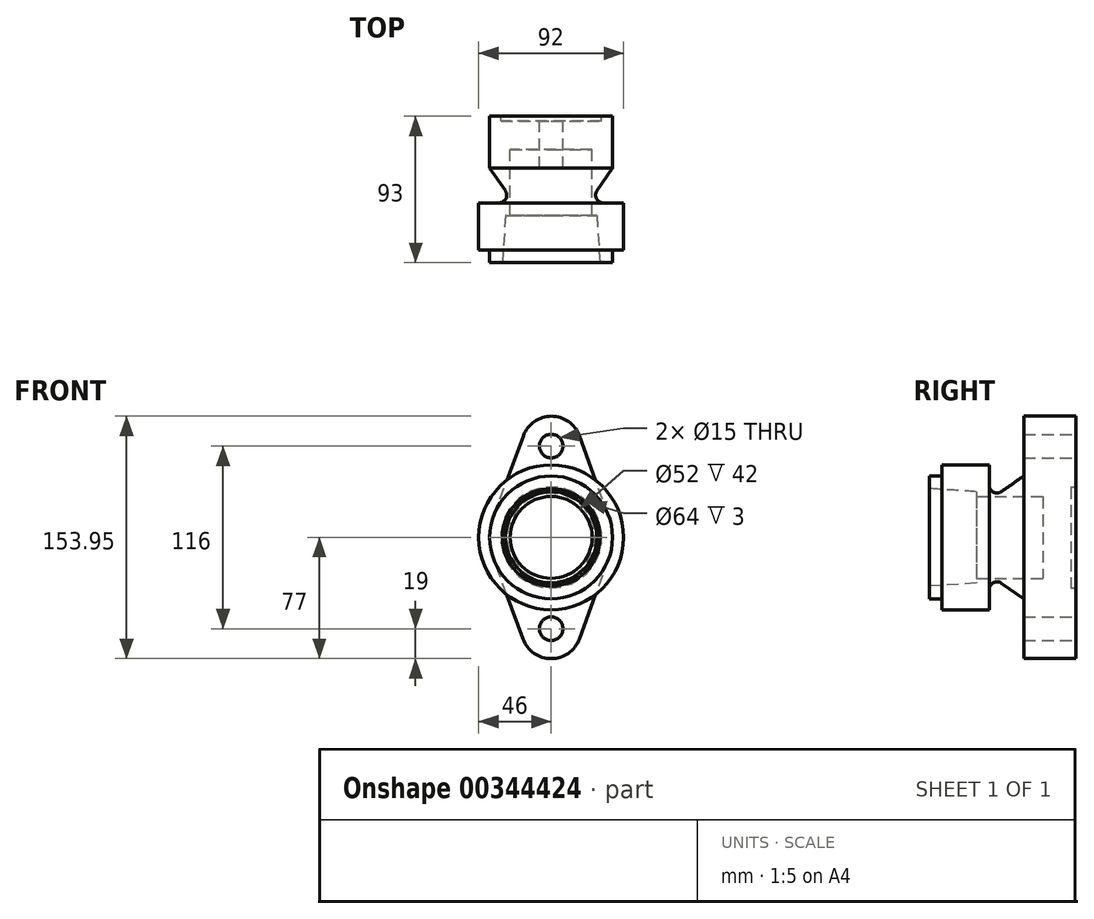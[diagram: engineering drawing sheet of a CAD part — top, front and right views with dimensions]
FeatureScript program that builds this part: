
annotation { "Feature Type Name" : "Feature", "Feature Type Description" : "" }
export const myFeature = defineFeature(function(context is Context, id is Id, definition is map)
    precondition{}
    {
        {
            var Q0;
            Q0=qCreatedBy(makeId("Right.planeOp"),FACE);
            var sketch = newSketch(context, id + "F0", { "sketchPlane" : qUnion([Q0])});
            skLineSegment(sketch, "E0", {"start": v(0, 0) * mm, "end": v(18, 0) * mm});
            skLineSegment(sketch, "E1", {"start": v(18, 0) * mm, "end": v(18, 32) * mm});
            skLineSegment(sketch, "E2", {"start": v(18, 32) * mm, "end": v(21, 32) * mm});
            skLineSegment(sketch, "E3", {"start": v(21, 32) * mm, "end": v(21, 39) * mm});
            skLineSegment(sketch, "E4", {"start": v(-64, 46) * mm, "end": v(-64, 39) * mm});
            skLineSegment(sketch, "E5", {"start": v(-64, 39) * mm, "end": v(-72, 39) * mm});
            skLineSegment(sketch, "E6", {"start": v(-72, 39) * mm, "end": v(-72, 31) * mm});
            skPoint(sketch, "E7.end.orphan", {"position": v(-31.9, 0) * mm});
            skLineSegment(sketch, "E8", {"start": v(0, 0) * mm, "end": v(0, 26) * mm});
            skLineSegment(sketch, "E9", {"start": v(0, 26) * mm, "end": v(-42, 26) * mm});
            skLineSegment(sketch, "E10", {"start": v(-42, 26) * mm, "end": v(-42, 29) * mm});
            skLineSegment(sketch, "E11", {"start": v(-42, 29) * mm, "end": v(-72, 31) * mm});
            skLineSegment(sketch, "E12", {"start": v(21, 39) * mm, "end": v(-12, 39) * mm});
            skLineSegment(sketch, "E13", {"start": v(-64, 46) * mm, "end": v(-34, 46) * mm});
            skLineSegment(sketch, "E14", {"start": v(-34, 46) * mm, "end": v(-34, 33.2) * mm});
            skLineSegment(sketch, "E15", {"start": v(-12, 39) * mm, "end": v(-26.13, 29.1) * mm});
            skPoint(sketch, "E16.newPointA", {"position": v(-34, 35.38) * mm});
            skPoint(sketch, "E16.newPointB", {"position": v(-26.33, 28.97) * mm});
            skArc(sketch, "E16.filletArc", {"start": v(-34, 33.2) * mm, "mid": v(-31.3, 28.77) * mm, "end": v(-26.13, 29.1) * mm});
            skLineSegment(sketch, "E17", {"start": v(0, 0) * mm, "end": v(-82.73, 0) * mm, "construction": true});
            skSolve(sketch);
        }
        {
            var Q0;
            Q0=makeQuery(id+"F0.imprint","IMPRINT",FACE,{"disambiguationData":[TD([[makeQuery(id+"F0.imprint","IMPRINT",EDGE,{"derivedFrom":sQuery(id+"F0.wireOp",EDGE,"E0")}),1.0]])]});
            var Q1;
            Q1=sQuery(id+"F0.wireOp",EDGE,"E17");
            revolve(context, id + "F1", {"entities" : qUnion([Q0]), "axis" : qUnion([Q1]), "revolveType" : RevolveType.FULL});
        }
        {
            var Q0;
            Q0=makeQuery(id+"F1.opRevolve","SWEPT_FACE",FACE,{"disambiguationData":[OSD([sQuery(id+"F0.wireOp",EDGE,"E3")])]});
            var sketch = newSketch(context, id + "F2", { "sketchPlane" : qUnion([Q0])});
            skLineSegment(sketch, "E18", {"start": v(-58.5, 58) * mm, "end": v(55.5, 58) * mm, "construction": true});
            skLineSegment(sketch, "E19", {"start": v(0, 58) * mm, "end": v(0, -58) * mm, "construction": true});
            skLineSegment(sketch, "E20", {"start": v(0, -58) * mm, "end": v(-55.5, -58) * mm, "construction": true});
            skLineSegment(sketch, "E21", {"start": v(0, -58) * mm, "end": v(57.83, -58) * mm, "construction": true});
            skCircle(sketch, "E22", {"center": v(0, 58) * mm, "radius": 7.5 * mm});
            skCircle(sketch, "E23", {"center": v(0, -58) * mm, "radius": 7.5 * mm});
            skArc(sketch, "E24", {"start": v(-17.83, -64.55) * mm, "mid": v(0, -77) * mm, "end": v(17.83, -64.55) * mm});
            skLineSegment(sketch, "E25.trimOffspring", {"start": v(41.55, 0) * mm, "end": v(42.04, 1.35) * mm});
            skLineSegment(sketch, "E26.trimOffspring", {"start": v(41.55, 0) * mm, "end": v(42.07, -1.43) * mm});
            skArc(sketch, "E27", {"start": v(-36.6, -13.45) * mm, "mid": v(0, -39) * mm, "end": v(36.6, -13.45) * mm});
            skLineSegment(sketch, "E28", {"start": v(17.83, -64.55) * mm, "end": v(36.6, -13.45) * mm});
            skLineSegment(sketch, "E29", {"start": v(36.57, 13.55) * mm, "end": v(17.67, 64.55) * mm});
            skLineSegment(sketch, "E30", {"start": v(-36.64, 13.37) * mm, "end": v(-18, 64.46) * mm});
            skLineSegment(sketch, "E31", {"start": v(-36.6, -13.45) * mm, "end": v(-17.83, -64.55) * mm});
            skLineSegment(sketch, "E32.trimOffspring", {"start": v(41.55, 0) * mm, "end": v(41.57, 0.06) * mm});
            skArc(sketch, "E33.trimOffspring", {"start": v(17.67, 64.55) * mm, "mid": v(-0.2, 76.95) * mm, "end": v(-18, 64.46) * mm});
            skArc(sketch, "E34.trimOffspring", {"start": v(36.57, 13.55) * mm, "mid": v(-0.1, 39) * mm, "end": v(-36.64, 13.37) * mm});
            skSolve(sketch);
        }
        {
            var Q0;
            Q0=makeQuery(id+"F2.imprint","IMPRINT",FACE,{"disambiguationData":[TD([[makeQuery(id+"F2.imprint","IMPRINT",EDGE,{"derivedFrom":sQuery(id+"F2.wireOp",EDGE,"E22")}),-1.0]])]});
            var Q1;
            Q1=makeQuery(id+"F2.imprint","IMPRINT",FACE,{"disambiguationData":[TD([[makeQuery(id+"F2.imprint","IMPRINT",EDGE,{"derivedFrom":sQuery(id+"F2.wireOp",EDGE,"E23")}),-1.0]])]});
            extrude(context, id + "F3", {"entities" : qUnion([Q0, Q1]), "operationType" : NewBodyOperationType.ADD, "oppositeDirection" : true, "depth" : 33 * mm});
        }
    });
